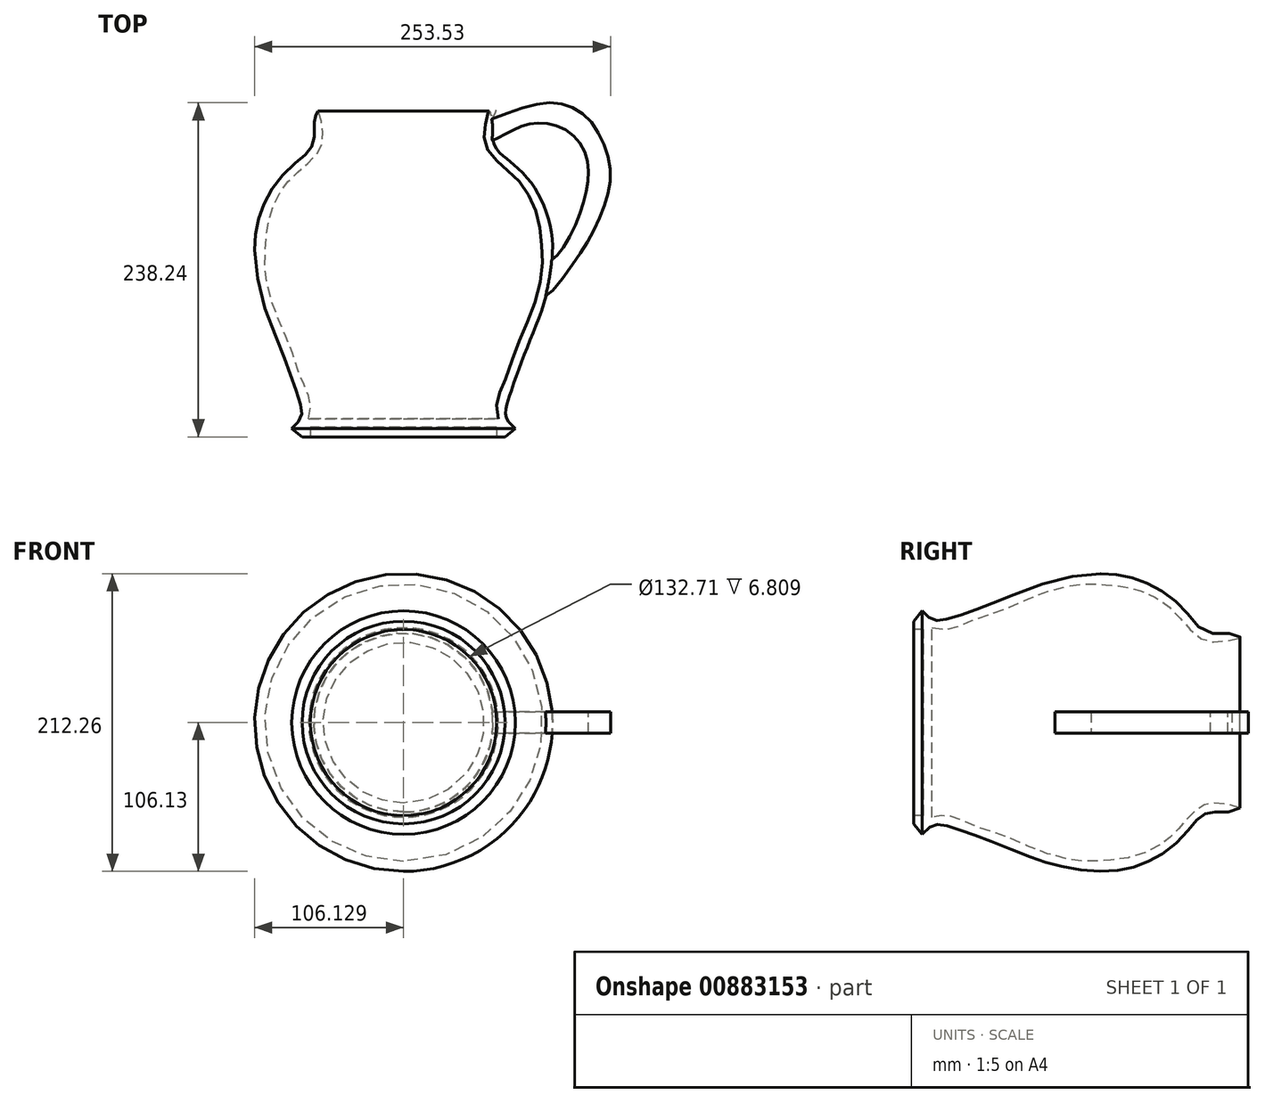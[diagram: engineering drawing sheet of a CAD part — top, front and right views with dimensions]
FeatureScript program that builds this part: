
annotation { "Feature Type Name" : "Feature", "Feature Type Description" : "" }
export const myFeature = defineFeature(function(context is Context, id is Id, definition is map)
    precondition{}
    {
        {
            var Q0;
            Q0=qCreatedBy(makeId("Top.planeOp"),FACE);
            var sketch = newSketch(context, id + "F0", { "sketchPlane" : qUnion([Q0])});
            skLineSegment(sketch, "E0", {"start": v(36.86, -36.27) * mm, "end": v(103.21, -36.27) * mm});
            skLineSegment(sketch, "E1", {"start": v(103.21, -36.27) * mm, "end": v(103.21, -43.08) * mm});
            skLineSegment(sketch, "E2", {"start": v(103.21, -43.08) * mm, "end": v(109.1, -43.08) * mm});
            skLineSegment(sketch, "E3", {"start": v(109.1, -43.08) * mm, "end": v(116.5, -37.15) * mm});
            skLineSegment(sketch, "E4", {"start": v(36.86, -36.27) * mm, "end": v(36.86, -30.03) * mm});
            skFitSpline(sketch, "E5", {"points": [v(116.5, -37.15) * mm, v(111.37, -31.67) * mm, v(109.51, -26.96) * mm, v(110.13, -21.12) * mm, v(114.23, -7.97) * mm, v(120.8, 10.28) * mm, v(132.49, 39.79) * mm, v(138.16, 57.04) * mm, v(142.65, 83.27) * mm, v(141.7, 105.96) * mm, v(136.24, 123.06) * mm, v(126.26, 140) * mm, v(110.83, 154.82) * mm, v(103.87, 161.18) * mm, v(100.54, 168.74) * mm, v(100.84, 176.9) * mm, v(97.82, 189.31) * mm, v(94.5, 173.88) * mm, v(94.8, 165.71) * mm, v(99.33, 157.85) * mm, v(107.8, 149.68) * mm, v(116.5, 141.82) * mm, v(123.53, 133.35) * mm, v(132.6, 112.47) * mm, v(135.33, 89.78) * mm, v(135.63, 76.47) * mm, v(129.14, 48.69) * mm, v(116.5, 18.46) * mm, v(111.68, 3.16) * mm, v(103.98, -15.32) * mm, v(103.21, -22.88) * mm, v(104.47, -30.03) * mm], "startDerivative": vector(-251.54, 236.58) * mm, "endDerivative": vector(207.16, -305.42) * mm});
            skLineSegment(sketch, "E6", {"start": v(36.86, -30.03) * mm, "end": v(104.47, -30.03) * mm});
            skSolve(sketch);
        }
        {
            var Q0;
            Q0=makeQuery(id+"F0.imprint","IMPRINT",FACE,{"disambiguationData":[TD([[makeQuery(id+"F0.imprint","IMPRINT",EDGE,{"derivedFrom":sQuery(id+"F0.wireOp",EDGE,"E0")}),1.0]])]});
            var Q1;
            Q1=sQuery(id+"F0.wireOp",EDGE,"E4");
            revolve(context, id + "F1", {"surfaceOperationType" : NewSurfaceOperationType.NEW, "entities" : qUnion([Q0]), "axis" : qUnion([Q1]), "revolveType" : RevolveType.FULL});
        }
        {
            var Q0;
            Q0=qCreatedBy(makeId("Top.planeOp"),FACE);
            var sketch = newSketch(context, id + "F2", { "sketchPlane" : qUnion([Q0])});
            skLineSegment(sketch, "E7", {"start": v(138.39, 81.43) * mm, "end": v(138.39, 69.02) * mm});
            skLineSegment(sketch, "E8", {"start": v(138.39, 69.02) * mm, "end": v(135.43, 60.74) * mm});
            skFitSpline(sketch, "E9", {"points": [v(135.43, 60.74) * mm, v(138.04, 57.36) * mm, v(154.7, 76.36) * mm, v(169.53, 98.75) * mm, v(179.98, 121.9) * mm, v(184.26, 142.94) * mm, v(179.9, 164.72) * mm, v(168.43, 183.7) * mm, v(152.05, 193.83) * mm, v(131.3, 193.96) * mm, v(97.8, 182.67) * mm], "startDerivative": vector(42.5, -115.4) * mm, "endDerivative": vector(-265.1, -112.2) * mm});
            skLineSegment(sketch, "E10", {"start": v(97.8, 182.67) * mm, "end": v(97.8, 167.09) * mm});
            skFitSpline(sketch, "E11", {"points": [v(97.8, 167.09) * mm, v(105.2, 170.6) * mm, v(120, 178) * mm, v(135.58, 180.72) * mm, v(154.27, 174.49) * mm, v(166.74, 158.13) * mm, v(167.9, 136.7) * mm, v(160.11, 110.22) * mm, v(145.31, 85.3) * mm, v(138.39, 81.43) * mm], "startDerivative": vector(89.56, 39.76) * mm, "endDerivative": vector(-89.5, -29.7) * mm});
            skSolve(sketch);
        }
        {
            var Q0;
            Q0=makeQuery(id+"F2.imprint","IMPRINT",FACE,{"disambiguationData":[TD([[makeQuery(id+"F2.imprint","IMPRINT",EDGE,{"derivedFrom":sQuery(id+"F2.wireOp",EDGE,"E7")}),1.0]])]});
            extrude(context, id + "F3", {"entities" : qUnion([Q0]), "operationType" : NewBodyOperationType.ADD, "endBound" : BoundingType.SYMMETRIC, "depth" : 15 * mm, "offsetDistance" : 25 * mm});
        }
    });
